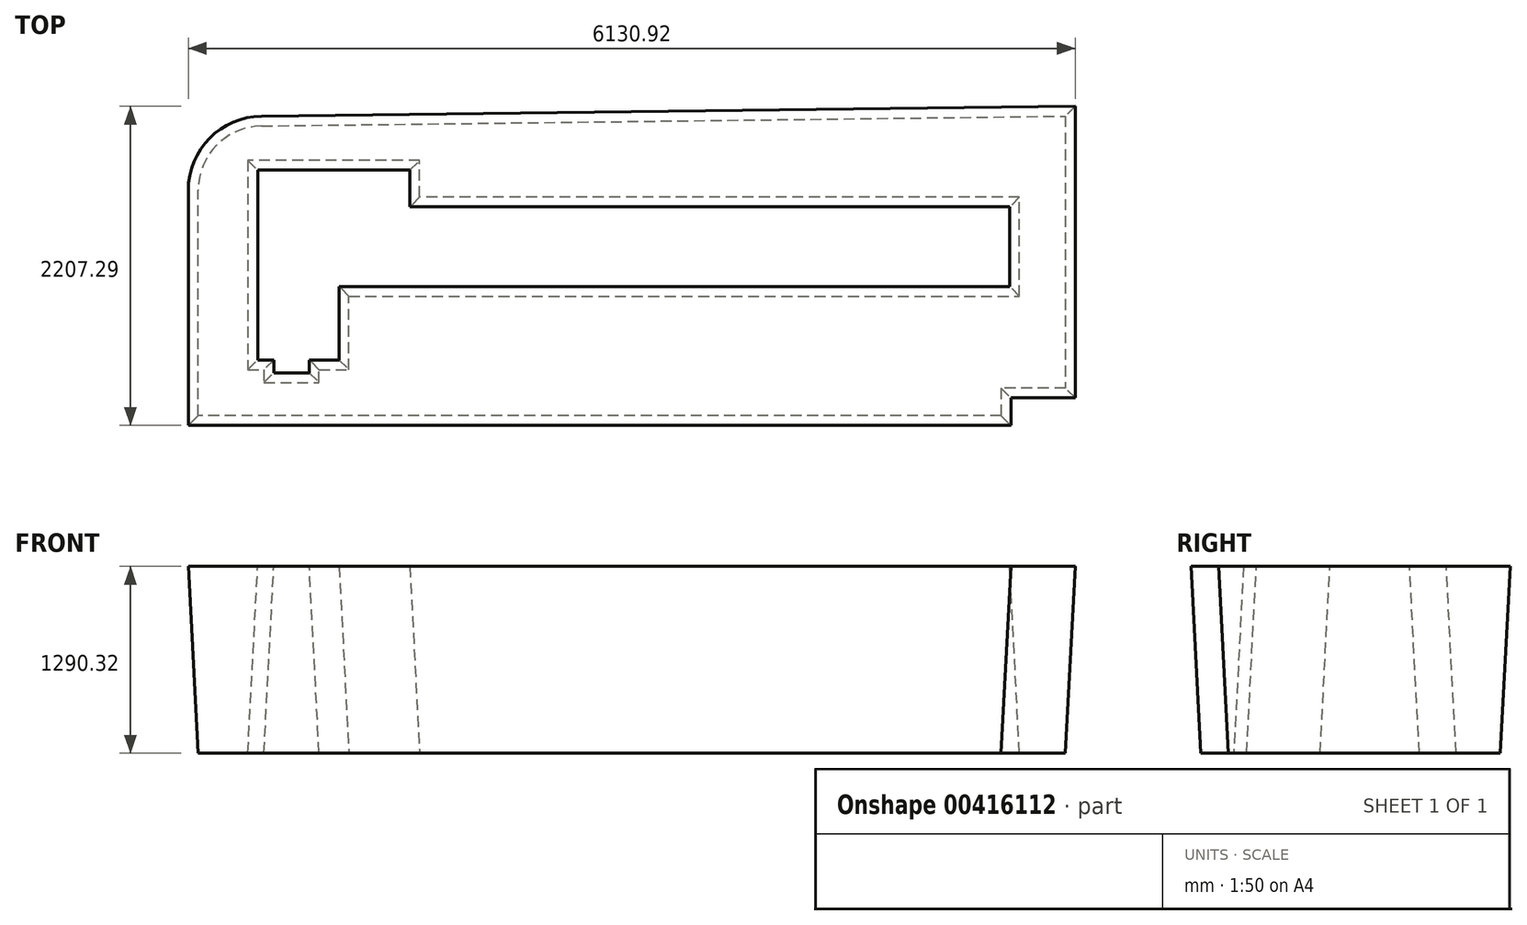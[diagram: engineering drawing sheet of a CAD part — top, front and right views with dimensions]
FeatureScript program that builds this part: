
annotation { "Feature Type Name" : "Feature", "Feature Type Description" : "" }
export const myFeature = defineFeature(function(context is Context, id is Id, definition is map)
    precondition{}
    {
        {
            var Q0;
            Q0=qCreatedBy(makeId("Top.planeOp"),FACE);
            var sketch = newSketch(context, id + "F0", { "sketchPlane" : qUnion([Q0])});
            skLineSegment(sketch, "E0.top", {"start": v(2553.34, -998.98) * mm, "end": v(-2997.83, -998.98) * mm});
            skLineSegment(sketch, "E0.left", {"start": v(2997.84, 998.98) * mm, "end": v(2997.84, -998.98) * mm});
            skLineSegment(sketch, "E0.right", {"start": v(-2997.83, 560.38) * mm, "end": v(-2997.83, -998.98) * mm});
            skPoint(sketch, "E0.middle", {"position": v(0, 0) * mm});
            skLineSegment(sketch, "E1", {"start": v(-2559.27, 1004.34) * mm, "end": v(2997.83, 1072.24) * mm});
            skLineSegment(sketch, "E2", {"start": v(2997.83, 1072.24) * mm, "end": v(2997.83, 998.98) * mm});
            skLineSegment(sketch, "E3.bottom", {"start": v(-2653.66, -681.48) * mm, "end": v(-2542.16, -681.48) * mm});
            skLineSegment(sketch, "E3.top", {"start": v(-2653.66, 512.32) * mm, "end": v(-2653.66, 512.32) * mm});
            skLineSegment(sketch, "E3.left", {"start": v(-2653.66, -681.48) * mm, "end": v(-2653.66, 512.32) * mm});
            skLineSegment(sketch, "E3.right", {"start": v(2680.34, -173.48) * mm, "end": v(2680.34, 512.32) * mm});
            skLineSegment(sketch, "E4.top", {"start": v(2997.84, -808.48) * mm, "end": v(2553.34, -808.48) * mm});
            skLineSegment(sketch, "E4.right", {"start": v(2553.34, -998.98) * mm, "end": v(2553.34, -808.48) * mm});
            skLineSegment(sketch, "E5.top", {"start": v(2680.34, -173.48) * mm, "end": v(-1955.16, -173.48) * mm});
            skLineSegment(sketch, "E5.right", {"start": v(-1955.16, -681.48) * mm, "end": v(-1955.16, -173.48) * mm});
            skLineSegment(sketch, "E6.top", {"start": v(-1466.21, 766.32) * mm, "end": v(-2653.66, 766.32) * mm});
            skLineSegment(sketch, "E6.left", {"start": v(-1466.21, 512.32) * mm, "end": v(-1466.21, 766.32) * mm});
            skLineSegment(sketch, "E6.right", {"start": v(-2653.66, 512.32) * mm, "end": v(-2653.66, 766.32) * mm});
            skLineSegment(sketch, "E7.top", {"start": v(-2161.16, -770.38) * mm, "end": v(-2542.16, -770.38) * mm});
            skLineSegment(sketch, "E7.left", {"start": v(-2161.16, -681.48) * mm, "end": v(-2161.16, -770.38) * mm});
            skLineSegment(sketch, "E7.right", {"start": v(-2542.16, -681.48) * mm, "end": v(-2542.16, -770.38) * mm});
            skLineSegment(sketch, "E8.trimOffspring", {"start": v(-2161.16, -681.48) * mm, "end": v(-1955.16, -681.48) * mm});
            skLineSegment(sketch, "E9.trimOffspring", {"start": v(-1466.21, 512.32) * mm, "end": v(2680.34, 512.32) * mm});
            skPoint(sketch, "E10.visualSharp", {"position": v(-2997.83, 998.98) * mm});
            skArc(sketch, "E10.filletArc", {"start": v(-2559.27, 1004.34) * mm, "mid": v(-2869.7, 872.4) * mm, "end": v(-2997.83, 560.38) * mm});
            skSolve(sketch);
        }
        {
            var Q0;
            Q0=makeQuery(id+"F0.imprint","IMPRINT",FACE,{"disambiguationData":[TD([[makeQuery(id+"F0.imprint","IMPRINT",EDGE,{"derivedFrom":sQuery(id+"F0.wireOp",EDGE,"E0.top")}),-1.0]])]});
            extrude(context, id + "F1", {"entities" : qUnion([Q0]), "depth" : 1290.32 * mm, "hasDraft" : true, "draftAngle" : 3 * degree});
        }
    });
